# Revit family: ledflood-e3_re300-150w-840-bl-n_709000117100
name_source: partatom
category: Lighting Fixtures
units: mm (PartAtom-declared; Revit-internal decimal feet)

## family parameters
Cut with Voids When Loaded = No
Host = Face
Light Source = No
Part Type = Normal
Room Calculation Point = No
Round Connector Dimension = Use Diameter
Shared = No

## types (1)
- LEDFlood-E3 Re300-150W-840-BL-N (1 x LED, 22500 lm, 4000)
    Apparent Load = 150 VA
    CIE Flux Codes = 70 93 99 100 100
    Color Rendering = 80
    Color Temperature = 4000
    Control Gear = Electronic ballast
    Default Elevation = 1800 mm
    Description = Floodlight EcoMax G3 150W-22500lm-4000K
    Height = 45 mm
    Lamp = 1 x LED
    Lamp Light Flux = 22500 lm
    Lamp count = 1
    Length = 350 mm
    Luminous efficacy = 150 lm/W
    Manufacturer = OPPLE
    ModVariant = No
    Model = 709000117100
    Mounting Place = Ceiling
    Mounting Type = Surface mounted
    Number of Poles = 1
    OnlyDefault = Yes
    Power Factor = 1
    Product Name = LEDFlood-E3 Re300-150W-840-BL-N
    Product group = Ceiling Light Luna
    ProductGroupID = 305
    Protection Class = Protection class I
    Protection Degree = IP 66
    RLX_Detail_Level = 1
    RLX_Emergency_Light_Flux = 0 lm
    RLX_Emergency_Type = 0
    RLX_Emergency_Type_DB = No
    RlxData = <blob elided: 258065 chars, md5=3c999a83>
    Socket = socket
    Standby Power = 0 W
    System Light Flux = 22500 lm
    System Power = 150 W
    Type Comments = Product without accessories
    Type Image = web_fl_eco_g3_n.jpg
    URL = http://relux.com
    VarID = ---
    Voltage = 0 V
    Weight = 0.00 kg
    Width = 288 mm

## geometry (parser evidence)
native form markers: Blend x4, Sweep x9
no freeform markers — native parametric forms only
